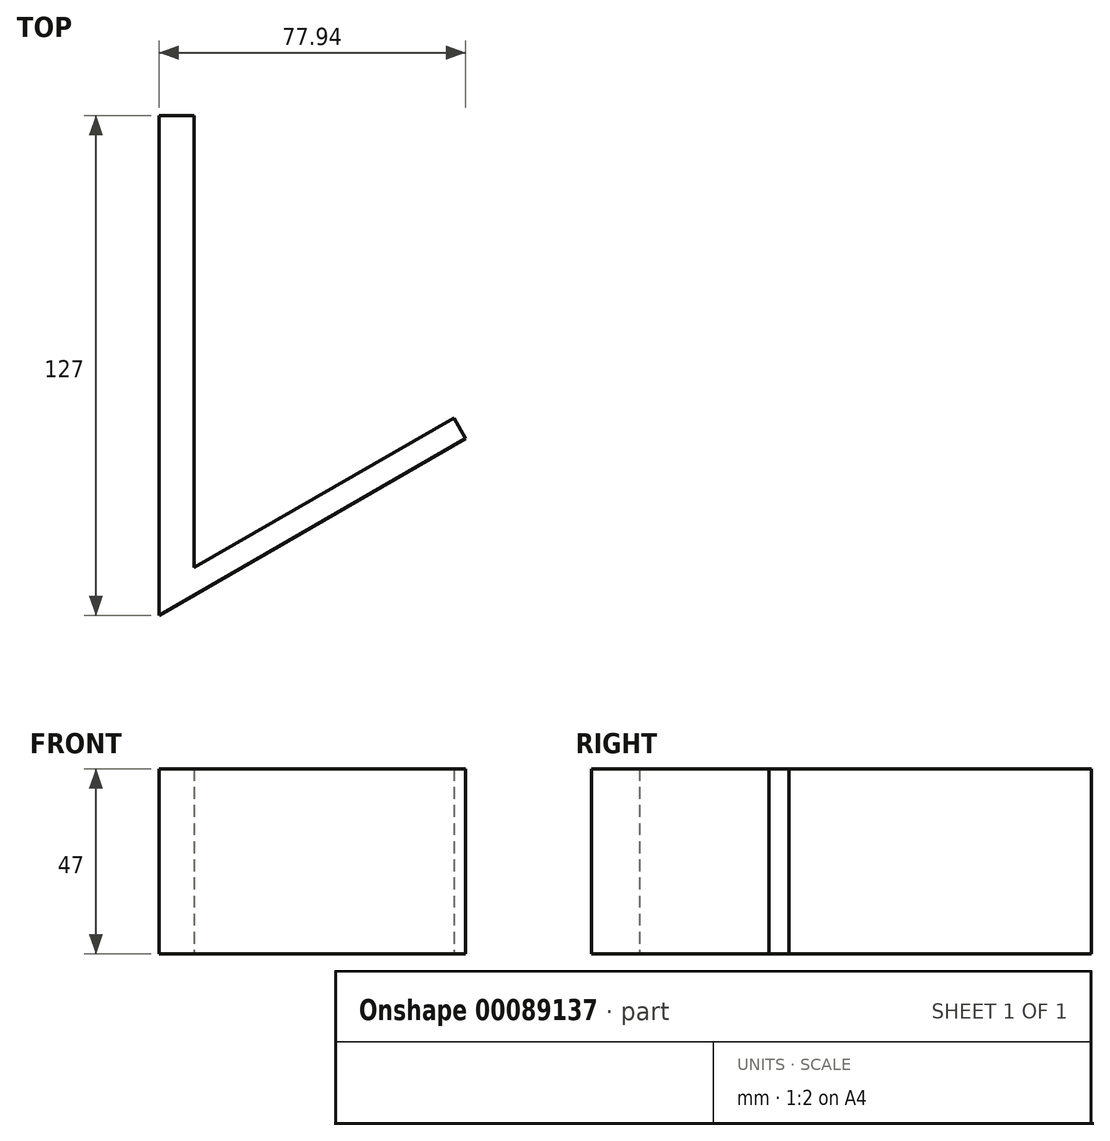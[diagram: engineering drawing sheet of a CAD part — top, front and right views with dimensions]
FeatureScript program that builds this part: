
annotation { "Feature Type Name" : "Feature", "Feature Type Description" : "" }
export const myFeature = defineFeature(function(context is Context, id is Id, definition is map)
    precondition{}
    {
        {
            var Q0;
            Q0=qCreatedBy(makeId("Top.planeOp"),FACE);
            var sketch = newSketch(context, id + "F0", { "sketchPlane" : qUnion([Q0])});
            skLineSegment(sketch, "E0.bottom", {"start": v(0, 0) * mm, "end": v(9, 0) * mm});
            skLineSegment(sketch, "E0.top", {"start": v(0, 127) * mm, "end": v(9, 127) * mm});
            skLineSegment(sketch, "E0.left", {"start": v(0, 0) * mm, "end": v(0, 127) * mm});
            skLineSegment(sketch, "E0.right", {"start": v(9, 0) * mm, "end": v(9, 127) * mm});
            skLineSegment(sketch, "E1", {"start": v(0, 0) * mm, "end": v(36.7, 0) * mm});
            skPoint(sketch, "E1.endSnap0", {"position": v(4.5, 0) * mm});
            skLineSegment(sketch, "E2", {"start": v(0, 0) * mm, "end": v(77.94, 45) * mm});
            skLineSegment(sketch, "E3", {"start": v(77.94, 45) * mm, "end": v(74.94, 50.2) * mm});
            skLineSegment(sketch, "E4", {"start": v(74.94, 50.2) * mm, "end": v(9, 12.12) * mm});
            skSolve(sketch);
        }
        {
            var Q0;
            {var subQ1=sQuery(id+"F0.wireOp",EDGE,"E0.top");Q0=makeQuery(id+"F0.imprint","IMPRINT",FACE,{"disambiguationData":[TD([[makeQuery(id+"F0.imprint","IMPRINT",EDGE,{"derivedFrom":subQ1}),-1.0]])]});}
            var Q1;
            {var subQ4=sQuery(id+"F0.wireOp",EDGE,"E3");Q1=makeQuery(id+"F0.imprint","IMPRINT",FACE,{"disambiguationData":[TD([[makeQuery(id+"F0.imprint","IMPRINT",EDGE,{"derivedFrom":subQ4}),1.0]])]});}
            extrude(context, id + "F1", {"entities" : qUnion([Q0, Q1]), "depth" : 47 * mm});
        }
    });
